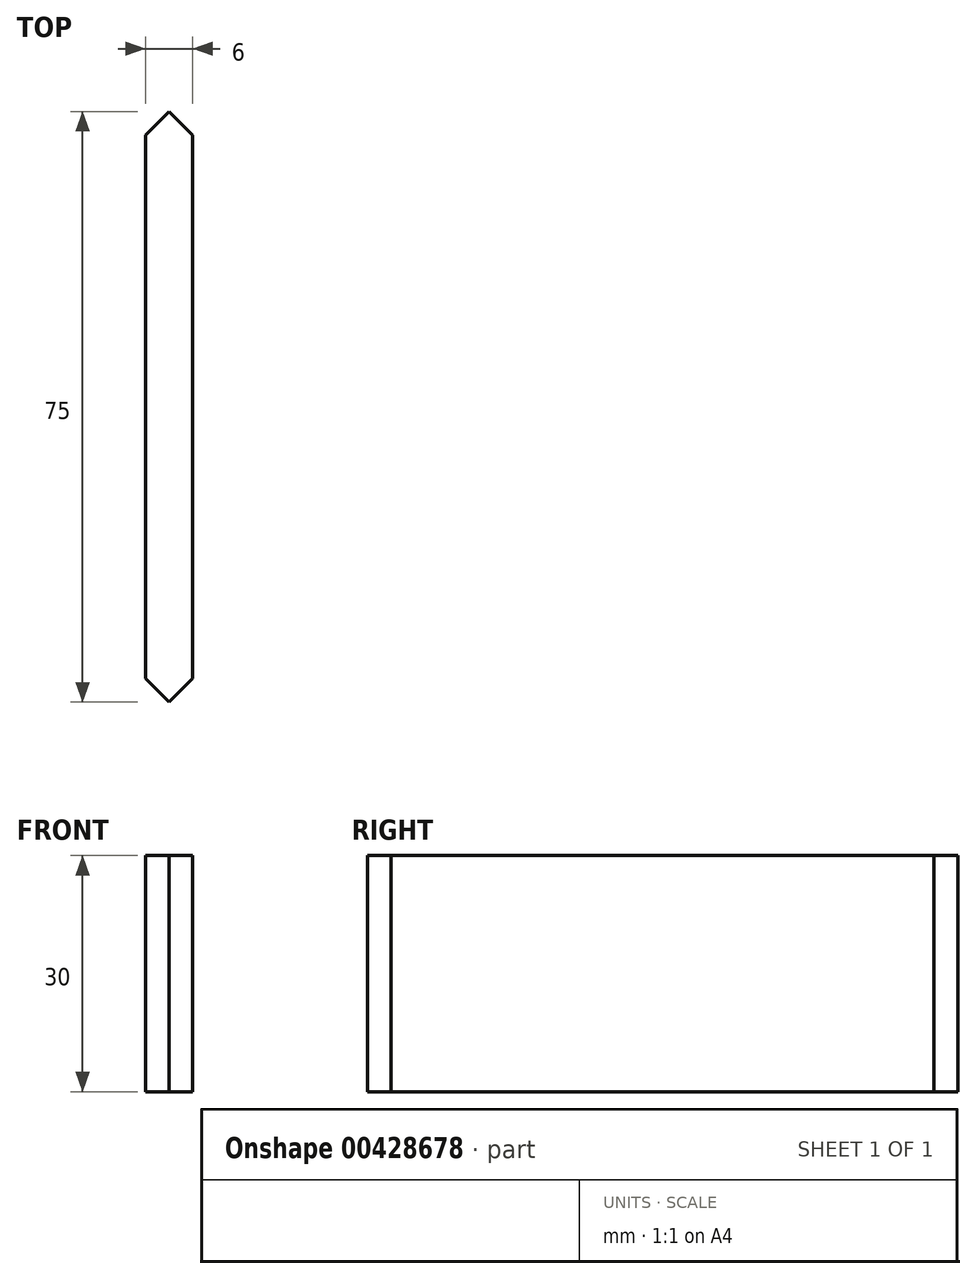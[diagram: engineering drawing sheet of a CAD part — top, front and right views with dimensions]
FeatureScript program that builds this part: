
annotation { "Feature Type Name" : "Feature", "Feature Type Description" : "" }
export const myFeature = defineFeature(function(context is Context, id is Id, definition is map)
    precondition{}
    {
        {
            var Q0;
            Q0=qCreatedBy(makeId("Right.planeOp"),FACE);
            var sketch = newSketch(context, id + "F0", { "sketchPlane" : qUnion([Q0])});
            skLineSegment(sketch, "E0.bottom", {"start": v(-37.5, 30) * mm, "end": v(37.5, 30) * mm});
            skLineSegment(sketch, "E0.top", {"start": v(-37.5, 0) * mm, "end": v(37.5, 0) * mm});
            skLineSegment(sketch, "E0.left", {"start": v(-37.5, 30) * mm, "end": v(-37.5, 0) * mm});
            skLineSegment(sketch, "E0.right", {"start": v(37.5, 30) * mm, "end": v(37.5, 0) * mm});
            skPoint(sketch, "E1", {"position": v(16.25, 0) * mm});
            skPoint(sketch, "E2", {"position": v(-16.25, 0) * mm});
            skSolve(sketch);
        }
        {
            var Q0;
            Q0 = qSketchRegion(id + "F0", true);
            extrude(context, id + "F1", {"entities" : qUnion([Q0]), "endBound" : BoundingType.SYMMETRIC, "depth" : 6 * mm});
        }
        {
            var Q0;
            Q0=makeQuery(id+"F1.opExtrude","CAP_EDGE",EDGE,{"disambiguationData":[OSD([sQuery(id+"F0.wireOp",EDGE,"E0.left")])],"isStart":false});
            var Q1;
            Q1=makeQuery(id+"F1.opExtrude","CAP_EDGE",EDGE,{"disambiguationData":[OSD([sQuery(id+"F0.wireOp",EDGE,"E0.left")])],"isStart":true});
            var Q2;
            Q2=makeQuery(id+"F1.opExtrude","CAP_EDGE",EDGE,{"disambiguationData":[OSD([sQuery(id+"F0.wireOp",EDGE,"E0.right")])],"isStart":true});
            var Q3;
            Q3=makeQuery(id+"F1.opExtrude","CAP_EDGE",EDGE,{"disambiguationData":[OSD([sQuery(id+"F0.wireOp",EDGE,"E0.right")])],"isStart":false});
            chamfer(context, id + "F2", {"entities" : qUnion([Q0, Q1, Q2, Q3]), "width" : 3 * mm, "tangentPropagation" : true});
        }
    });
